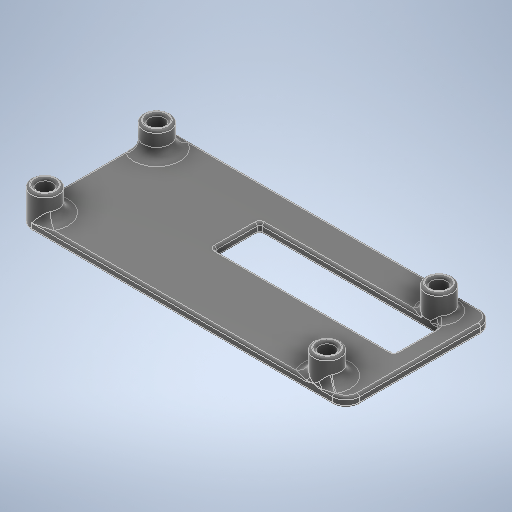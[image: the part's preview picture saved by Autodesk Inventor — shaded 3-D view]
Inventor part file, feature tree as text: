
AUTODESK INVENTOR PART (.ipt)
format: ipt  version: 2025 (Build 290162000, 162)  size: 566,784 bytes
history: native  units: mm
features: fillet x3, extrude x2, sketch x1
ambient origin geometry x8: Origin, YZ Plane, XZ Plane, XY Plane, X Axis, Y Axis, Z Axis, Center Point
bodies: Solid1 (feature_tree)
feature tree (6):
  sketch  "Sketch1"  dims[d0=3.2mm d1=58.0mm d2=23.0mm d3=5.5mm d7=2.0mm d8=0.0mm d9=5.0mm d10=0.0mm d11=0.5mm d12=37.0mm d13=9.4mm d15=2.75mm d16=4.65mm d17=6.65mm d18=11.95mm d19=0.0mm d20=2.0mm d21=1.0mm]
  extrude  "Extrusion1"  Depth=58.0mm
  extrude  "Extrusion2"  Depth=23.0mm
  fillet  "Fillet1"  Radius=5.5mm
  fillet  "Fillet2"  Radius=2.0mm
  fillet  "Fillet3"  Radius=5.0mm
